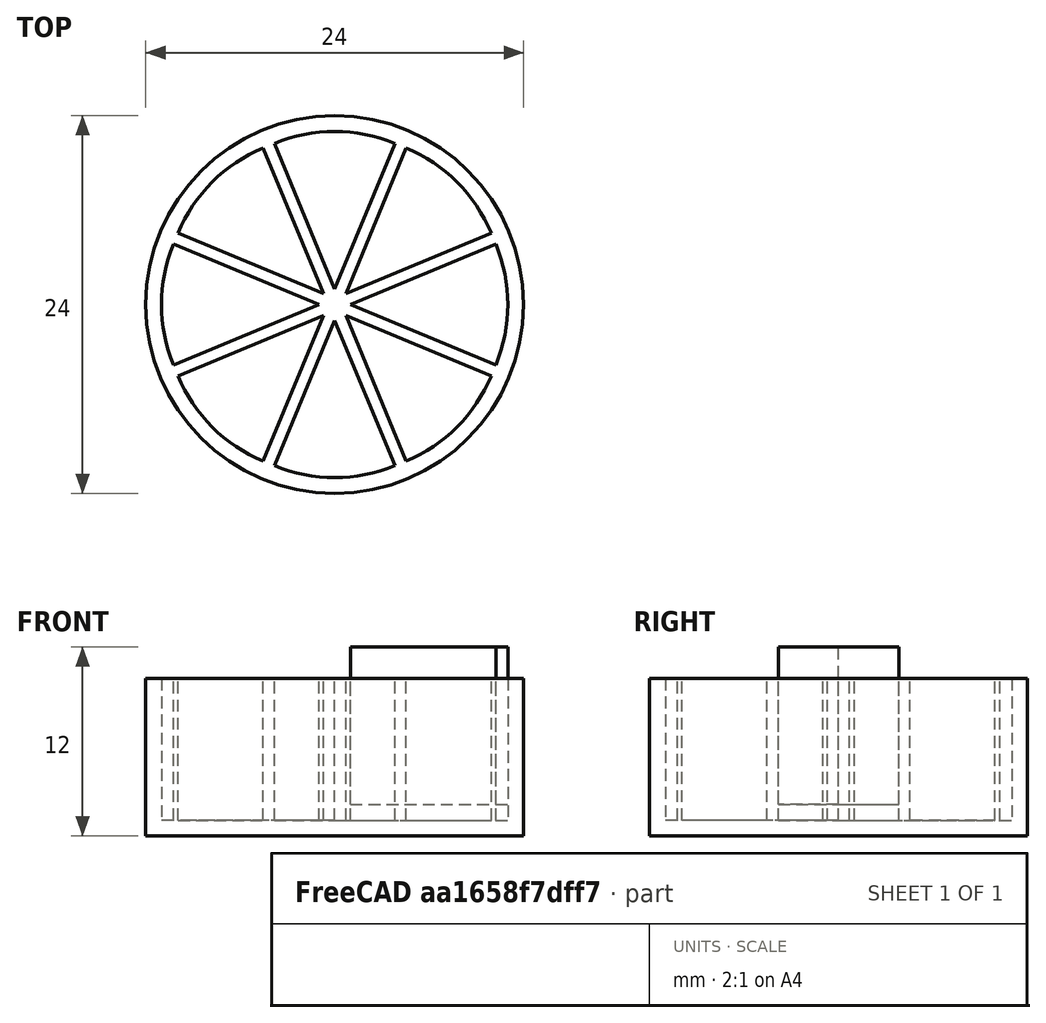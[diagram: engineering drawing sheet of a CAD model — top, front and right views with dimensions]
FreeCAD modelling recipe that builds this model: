
FCSTD DOCUMENT  (FreeCAD 1.0R39319 (Git))
Label: ojt1_t11r02_trivial
License: All rights reserved
LicenseURL: https://en.wikipedia.org/wiki/All_rights_reserved
objects: Part::Cylinder×3, Part::FeaturePython×1, Part::Cut×1
note: 4 computed .brp shape members not serialized (recipe doc carries the construction recipe); baked Part::Feature solids carry a one-line shape summary decoded from their .brp

FEATURE [Part::Cylinder] Cylinder  label="Cilindre"
  Angle = 360
  AttacherType = Attacher::AttachEngine3D
  FirstAngle = 0
  Height = 10
  Radius = 12
  SecondAngle = 0
FEATURE [Part::Cylinder] Cylinder001  label="Cilindre001"
  Angle = 45
  AttacherType = Attacher::AttachEngine3D
  FirstAngle = 0
  Height = 10
  Placement = pos=(1,0,2) rot=(0,0,1;-0.392699rad)
  Radius = 10
  SecondAngle = 0
FEATURE [Part::FeaturePython] Array  # Draft array (typed FeaturePython)
  AlwaysSyncPlacement = false
  Angle = 360
  ArrayType = 1
  Axis = (0,0,1)
  Base = -> Cylinder001
  Center = (0,0,0)
  Count = 8
  ExpandArray = false
  Fuse = false
  IntervalAxis = (0,0,0)
  IntervalX = (50,0,0)
  IntervalY = (0,50,0)
  IntervalZ = (0,0,50)
  NumberCircles = 3
  NumberPolar = 8
  NumberX = 2
  NumberY = 2
  NumberZ = 1
  Placement = pos=(0,0,-1) rot=(0,0,1;0rad)
  PlacementList = 8 placements: [(1,0,2),(0.707107,0.707107,2),(0,1,2),(-0.707107,0.707107,2),(-1,1.22465e-16,2),(-0.707107,-0.707107,2),(-2.22045e-16,-1,2),(0.707107,-0.707107,2)]
  RadialDistance = 50
  ScaleList = (8) [(1,1,1),(1,1,1),(1,1,1),(1,1,1),(1,1,1),(1,1,1),(1,1,1),(1,1,1)]
  Symmetry = 1
  TangentialDistance = 25
FEATURE [Part::Cut] Cut
  Base = -> Cylinder
  Refine = true
  Tool = -> Array
FEATURE [Part::Cylinder] Cylinder002  label="Cilindre002"
  Angle = 45
  AttacherType = Attacher::AttachEngine3D
  FirstAngle = 0
  Height = 10
  Placement = pos=(1,0,2) rot=(0,0,1;-0.392699rad)
  Radius = 10
  SecondAngle = 0
